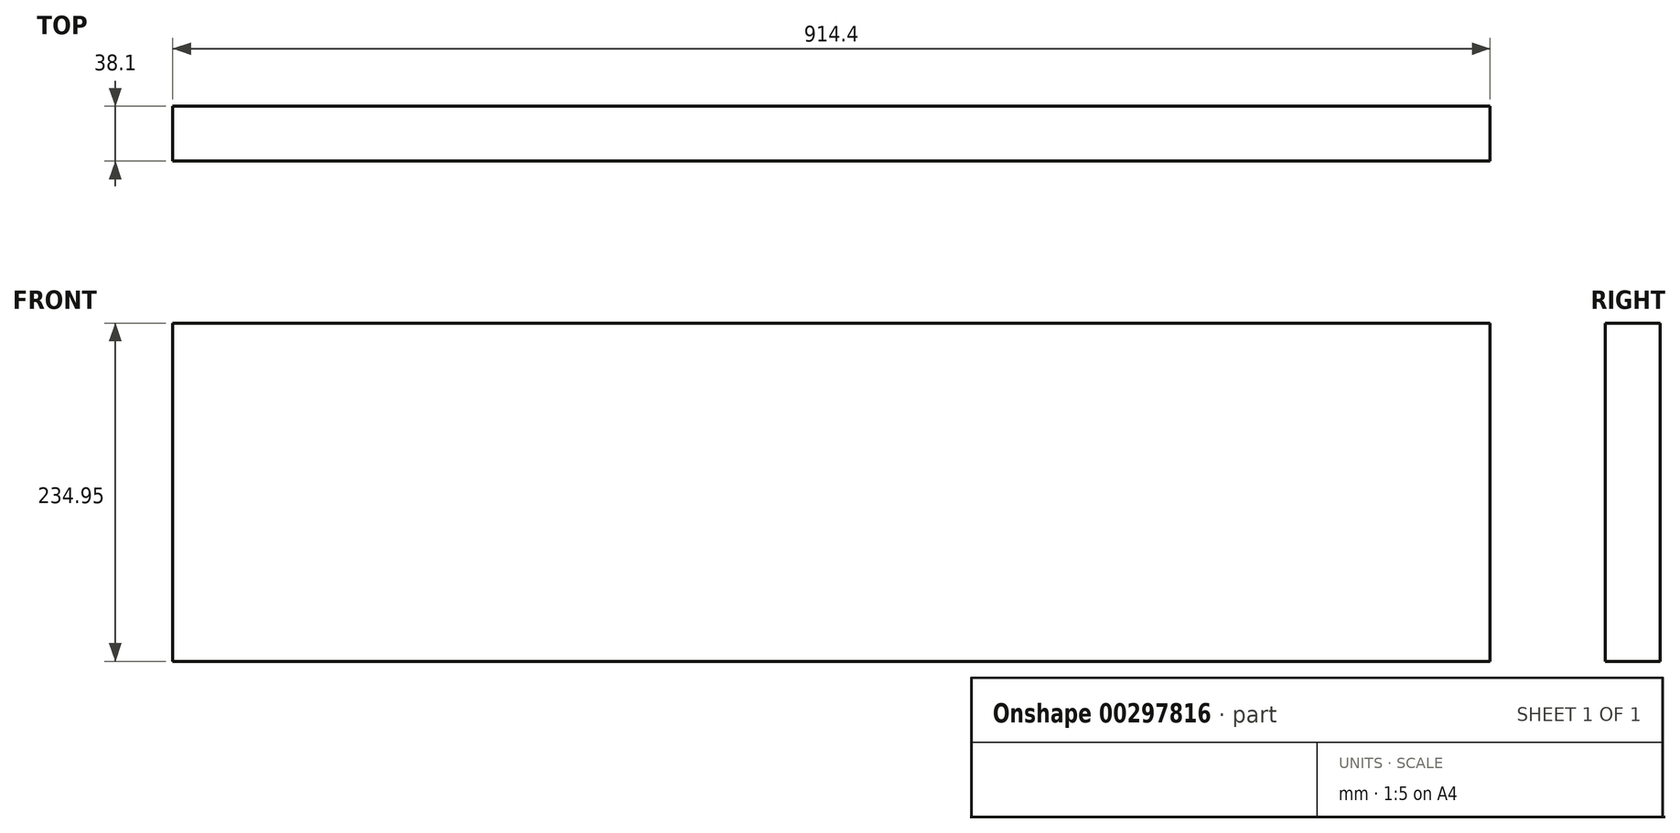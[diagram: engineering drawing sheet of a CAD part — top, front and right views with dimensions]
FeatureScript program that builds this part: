
annotation { "Feature Type Name" : "Feature", "Feature Type Description" : "" }
export const myFeature = defineFeature(function(context is Context, id is Id, definition is map)
    precondition{}
    {
        {
            var Q0;
            Q0=qCreatedBy(makeId("Front.planeOp"),FACE);
            var sketch = newSketch(context, id + "F0", { "sketchPlane" : qUnion([Q0])});
            skLineSegment(sketch, "E0.bottom", {"start": v(0, 0) * mm, "end": v(914.4, 0) * mm});
            skLineSegment(sketch, "E0.top", {"start": v(0, 234.95) * mm, "end": v(914.4, 234.95) * mm});
            skLineSegment(sketch, "E0.left", {"start": v(0, 0) * mm, "end": v(0, 234.95) * mm});
            skLineSegment(sketch, "E0.right", {"start": v(914.4, 0) * mm, "end": v(914.4, 234.95) * mm});
            skSolve(sketch);
        }
        {
            var Q0;
            Q0=makeQuery(id+"F0.imprint","IMPRINT",FACE,{"disambiguationData":[TD([[makeQuery(id+"F0.imprint","IMPRINT",EDGE,{"derivedFrom":sQuery(id+"F0.wireOp",EDGE,"E0.bottom")}),1.0]])]});
            extrude(context, id + "F1", {"entities" : qUnion([Q0]), "depth" : 38.1 * mm});
        }
    });
